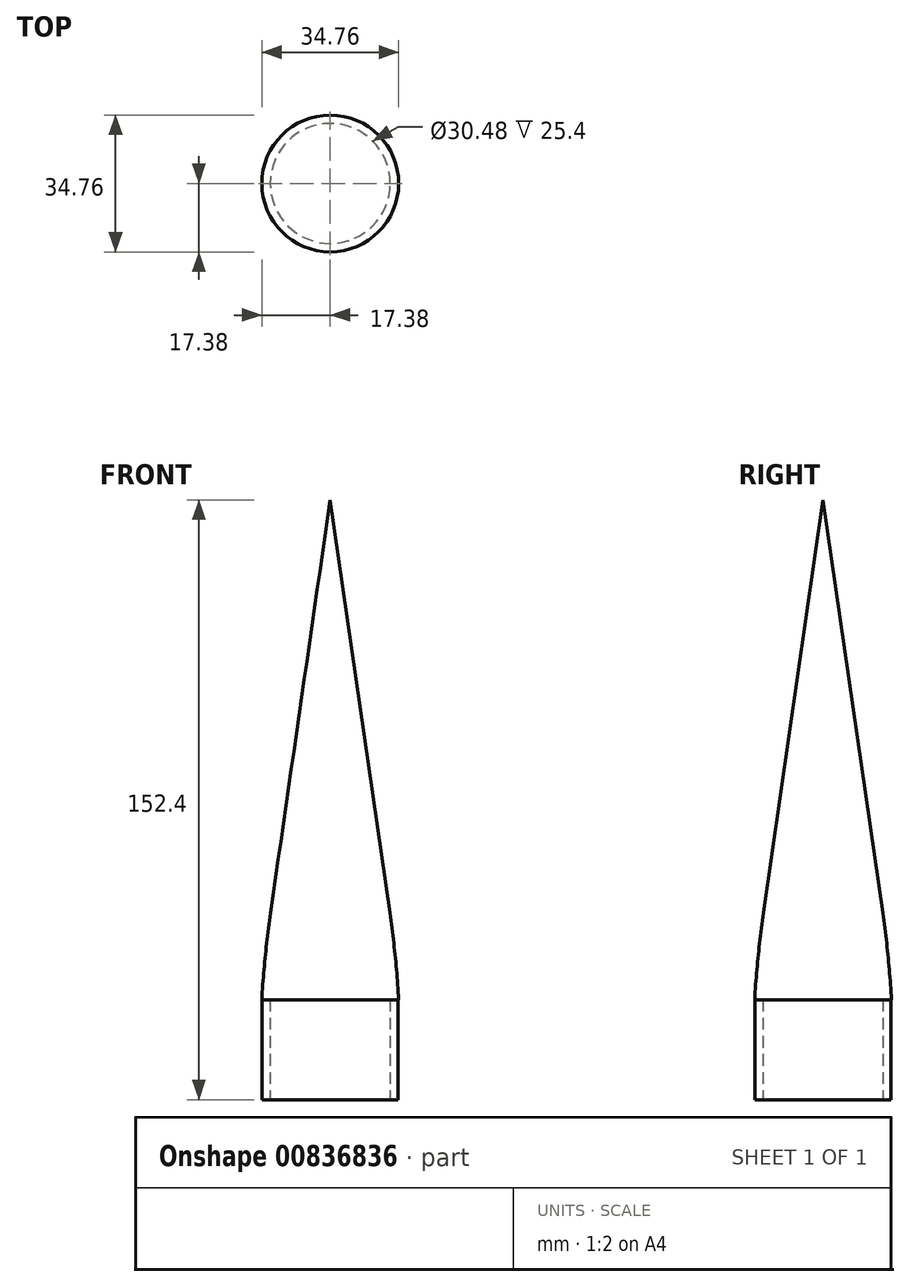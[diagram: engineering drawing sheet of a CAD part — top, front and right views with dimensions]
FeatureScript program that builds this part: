
annotation { "Feature Type Name" : "Feature", "Feature Type Description" : "" }
export const myFeature = defineFeature(function(context is Context, id is Id, definition is map)
    precondition{}
    {
        {
            var Q0;
            Q0=qCreatedBy(makeId("Front.planeOp"),FACE);
            var sketch = newSketch(context, id + "F0", { "sketchPlane" : qUnion([Q0])});
            skLineSegment(sketch, "E0", {"start": v(0, 0) * mm, "end": v(0, 177.8) * mm, "construction": true});
            skLineSegment(sketch, "E1", {"start": v(17.78, 0) * mm, "end": v(0, 0) * mm});
            skLineSegment(sketch, "E2", {"start": v(0, 0) * mm, "end": v(0, 152.4) * mm});
            skLineSegment(sketch, "E3", {"start": v(0, 152.4) * mm, "end": v(15.17, 47.39) * mm});
            skLineSegment(sketch, "E4", {"start": v(17.78, 11.07) * mm, "end": v(17.78, 0) * mm});
            skPoint(sketch, "E5.visualSharp", {"position": v(17.78, 29.32) * mm});
            skArc(sketch, "E5.filletArc", {"start": v(17.78, 11.07) * mm, "mid": v(17.13, 29.27) * mm, "end": v(15.17, 47.39) * mm});
            skSolve(sketch);
        }
        {
            var Q0;
            Q0=makeQuery(id+"F0.imprint","IMPRINT",FACE,{"disambiguationData":[TD([[makeQuery(id+"F0.imprint","IMPRINT",EDGE,{"derivedFrom":sQuery(id+"F0.wireOp",EDGE,"E1")}),-1.0]])]});
            var Q1;
            Q1=sQuery(id+"F0.wireOp",EDGE,"E0");
            revolve(context, id + "F1", {"surfaceOperationType" : NewSurfaceOperationType.NEW, "entities" : qUnion([Q0]), "axis" : qUnion([Q1]), "revolveType" : RevolveType.FULL});
        }
        {
            var Q0;
            Q0=makeQuery(id+"F1.opRevolve","SWEPT_FACE",FACE,{"disambiguationData":[OSD([sQuery(id+"F0.wireOp",EDGE,"E1")])]});
            var sketch = newSketch(context, id + "F2", { "sketchPlane" : qUnion([Q0])});
            skCircle(sketch, "E6", {"center": v(0, 0) * mm, "radius": 15.24 * mm});
            skSolve(sketch);
        }
        {
            var Q0;
            Q0 = qSketchRegion(id + "F2", true);
            extrude(context, id + "F3", {"entities" : qUnion([Q0]), "operationType" : NewBodyOperationType.REMOVE, "oppositeDirection" : true, "depth" : 25.4 * mm, "offsetDistance" : 25.4 * mm});
        }
        {
            var Q0;
            Q0=makeQuery(id+"F3.boolean.opBoolean","COPY",FACE,{"derivedFrom":makeQuery(id+"F3.opExtrude","CAP_FACE",FACE,{"disambiguationData":[OSD([sQuery(id+"F2.wireOp",EDGE,"E6")])],"isStart":false})});
            var sketch = newSketch(context, id + "F4", { "sketchPlane" : qUnion([Q0])});
            skCircle(sketch, "E7", {"center": v(0, 0) * mm, "radius": 17.78 * mm});
            skCircle(sketch, "E8", {"center": v(0, 0) * mm, "radius": 17.27 * mm});
            skSolve(sketch);
        }
        {
            var Q0;
            Q0 = qSketchRegion(id + "F4", true);
            extrude(context, id + "F5", {"entities" : qUnion([Q0]), "operationType" : NewBodyOperationType.REMOVE, "depth" : 25.4 * mm, "offsetDistance" : 25.4 * mm});
        }
    });
